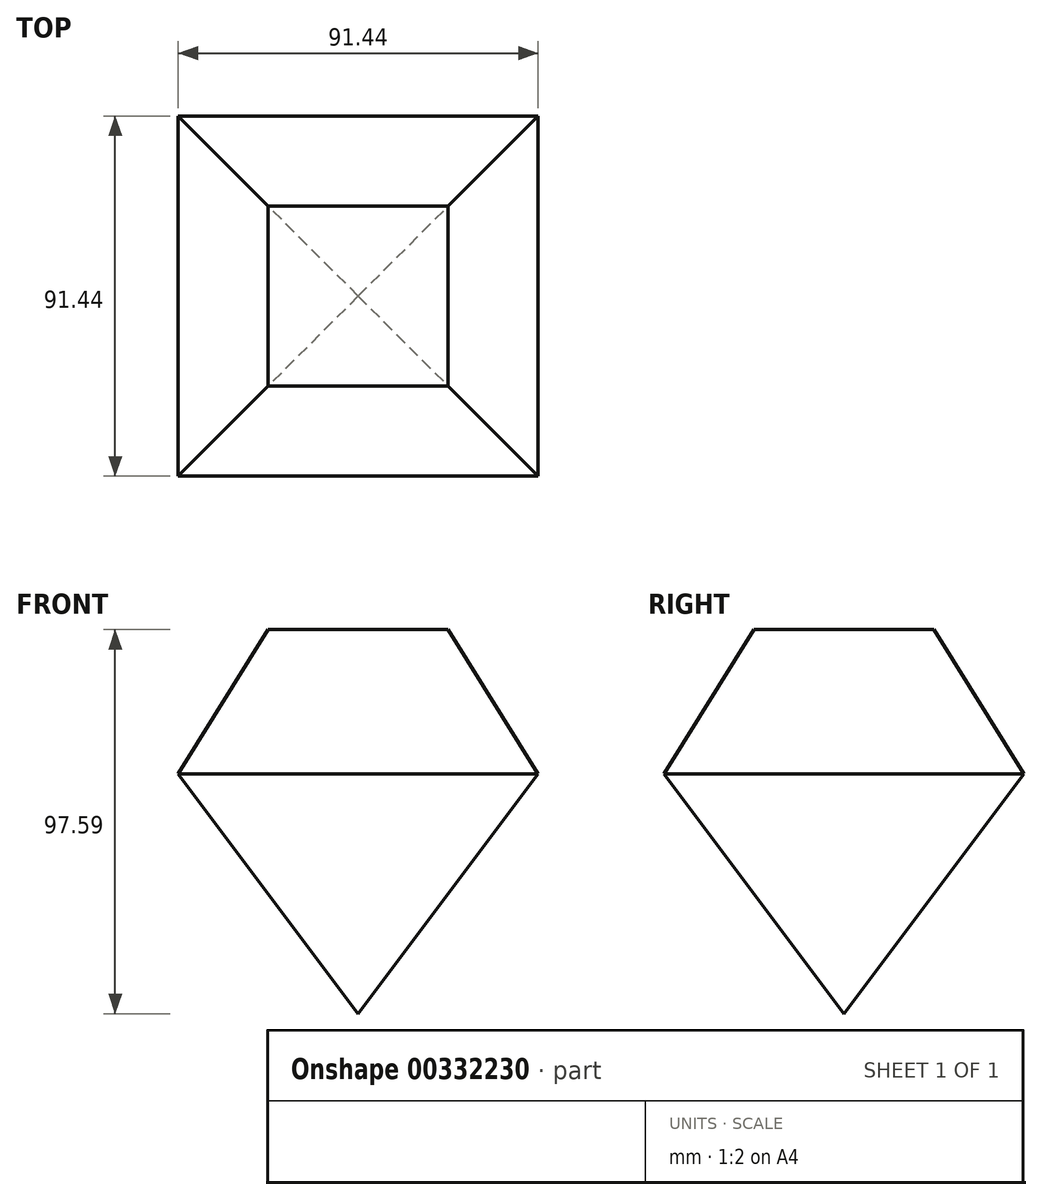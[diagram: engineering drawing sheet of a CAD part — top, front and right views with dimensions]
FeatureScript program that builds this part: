
annotation { "Feature Type Name" : "Feature", "Feature Type Description" : "" }
export const myFeature = defineFeature(function(context is Context, id is Id, definition is map)
    precondition{}
    {
        {
            var Q0;
            Q0=qCreatedBy(makeId("Front.planeOp"),FACE);
            var sketch = newSketch(context, id + "F0", { "sketchPlane" : qUnion([Q0])});
            skLineSegment(sketch, "E0.bottom", {"start": v(-45.72, 55.88) * mm, "end": v(45.72, 55.88) * mm});
            skLineSegment(sketch, "E0.top", {"start": v(-45.72, -60.96) * mm, "end": v(45.72, -60.96) * mm});
            skLineSegment(sketch, "E0.left", {"start": v(-45.72, 55.88) * mm, "end": v(-45.72, -60.96) * mm});
            skLineSegment(sketch, "E0.right", {"start": v(45.72, 55.88) * mm, "end": v(45.72, -60.96) * mm});
            skSolve(sketch);
        }
        {
            var Q0;
            Q0 = qSketchRegion(id + "F0", true);
            extrude(context, id + "F1", {"entities" : qUnion([Q0]), "depth" : 91.44 * mm});
        }
        {
            var Q0;
            Q0=makeQuery(id+"F1.opExtrude","CAP_FACE",FACE,{"disambiguationData":[OSD([sQuery(id+"F0.wireOp",EDGE,"E0.bottom"),sQuery(id+"F0.wireOp",EDGE,"E0.top"),sQuery(id+"F0.wireOp",EDGE,"E0.left"),sQuery(id+"F0.wireOp",EDGE,"E0.right")])],"isStart":false});
            var sketch = newSketch(context, id + "F2", { "sketchPlane" : qUnion([Q0])});
            skLineSegment(sketch, "E1", {"start": v(0, -60.96) * mm, "end": v(-45.72, 0) * mm});
            skLineSegment(sketch, "E2", {"start": v(0, -60.96) * mm, "end": v(45.72, 0) * mm});
            skLineSegment(sketch, "E3", {"start": v(-45.72, 0) * mm, "end": v(-22.86, 36.63) * mm});
            skLineSegment(sketch, "E4", {"start": v(45.72, 0) * mm, "end": v(22.86, 36.63) * mm});
            skLineSegment(sketch, "E5", {"start": v(-22.86, 36.63) * mm, "end": v(22.86, 36.63) * mm});
            skSolve(sketch);
        }
        {
            var Q0;
            Q0=makeQuery(id+"F1.opExtrude","SWEPT_FACE",FACE,{"disambiguationData":[OSD([sQuery(id+"F0.wireOp",EDGE,"E0.right")])]});
            var sketch = newSketch(context, id + "F3", { "sketchPlane" : qUnion([Q0])});
            skLineSegment(sketch, "E6", {"start": v(-45.72, -60.96) * mm, "end": v(-91.44, 0) * mm});
            skPoint(sketch, "E6.endSnap0", {"position": v(-91.44, -2.54) * mm});
            skLineSegment(sketch, "E7", {"start": v(-45.72, -60.96) * mm, "end": v(0, 0) * mm});
            skLineSegment(sketch, "E8", {"start": v(-91.44, 0) * mm, "end": v(-68.58, 36.63) * mm});
            skLineSegment(sketch, "E9", {"start": v(0, 0) * mm, "end": v(-22.86, 36.63) * mm});
            skLineSegment(sketch, "E10", {"start": v(-68.58, 36.63) * mm, "end": v(-22.86, 36.63) * mm});
            skSolve(sketch);
        }
        {
            var Q0;
            {var subQ2=sQuery(id+"F2.wireOp",EDGE,"E3");Q0=makeQuery(id+"F2.imprint","IMPRINT",FACE,{"disambiguationData":[TD([[makeQuery(id+"F2.imprint","IMPRINT",EDGE,{"derivedFrom":subQ2}),1.0]])]});}
            var Q1;
            {var subQ0=sQuery(id+"F2.wireOp",EDGE,"E2");Q1=makeQuery(id+"F2.imprint","IMPRINT",FACE,{"disambiguationData":[TD([[makeQuery(id+"F2.imprint","IMPRINT",EDGE,{"derivedFrom":subQ0}),-1.0]])]});}
            var Q2;
            {var subQ0=sQuery(id+"F2.wireOp",EDGE,"E1");Q2=makeQuery(id+"F2.imprint","IMPRINT",FACE,{"disambiguationData":[TD([[makeQuery(id+"F2.imprint","IMPRINT",EDGE,{"derivedFrom":subQ0}),1.0]])]});}
            extrude(context, id + "F4", {"entities" : qUnion([Q0, Q1, Q2]), "operationType" : NewBodyOperationType.REMOVE, "oppositeDirection" : true, "depth" : 127 * mm});
        }
        {
            var Q0;
            {var subQ3=sQuery(id+"F3.wireOp",EDGE,"E8");Q0=makeQuery(id+"F3.imprint","IMPRINT",FACE,{"disambiguationData":[TD([[makeQuery(id+"F3.imprint","IMPRINT",EDGE,{"derivedFrom":subQ3}),1.0]])]});}
            var Q1;
            {var subQ0=sQuery(id+"F3.wireOp",EDGE,"E7");Q1=makeQuery(id+"F3.imprint","IMPRINT",FACE,{"disambiguationData":[TD([[makeQuery(id+"F3.imprint","IMPRINT",EDGE,{"derivedFrom":subQ0}),-1.0]])]});}
            var Q2;
            {var subQ0=sQuery(id+"F3.wireOp",EDGE,"E6");Q2=makeQuery(id+"F3.imprint","IMPRINT",FACE,{"disambiguationData":[TD([[makeQuery(id+"F3.imprint","IMPRINT",EDGE,{"derivedFrom":subQ0}),1.0]])]});}
            extrude(context, id + "F5", {"entities" : qUnion([Q0, Q1, Q2]), "operationType" : NewBodyOperationType.REMOVE, "oppositeDirection" : true, "depth" : 152.4 * mm});
        }
    });
